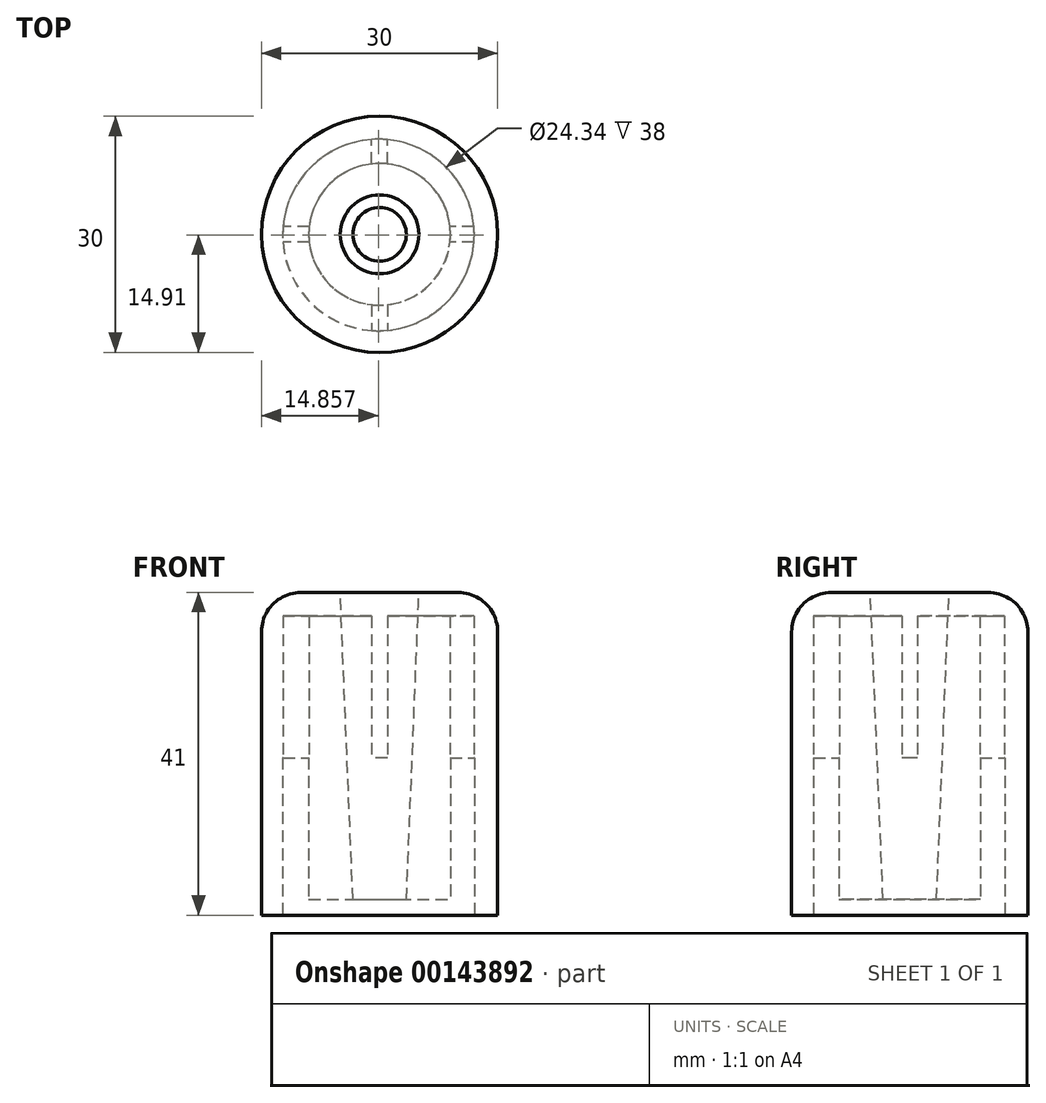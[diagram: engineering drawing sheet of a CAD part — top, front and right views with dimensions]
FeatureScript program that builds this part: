
annotation { "Feature Type Name" : "Feature", "Feature Type Description" : "" }
export const myFeature = defineFeature(function(context is Context, id is Id, definition is map)
    precondition{}
    {
        {
            var Q0;
            Q0=qCreatedBy(makeId("Top.planeOp"),FACE);
            var sketch = newSketch(context, id + "F0", { "sketchPlane" : qUnion([Q0])});
            skCircle(sketch, "E0", {"center": v(0, 0) * mm, "radius": 15 * mm});
            skCircle(sketch, "E1", {"center": v(-0.14, -0.1) * mm, "radius": 12.17 * mm});
            skSolve(sketch);
        }
        {
            var Q0;
            Q0=qSketchRegion(id+"F0",true);
            extrude(context, id + "F1", {"entities" : qUnion([Q0]), "depth" : 38 * mm});
        }
        {
            var Q0;
            Q0=makeQuery(id+"F1.opExtrude","CAP_FACE",FACE,{"disambiguationData":[OSD([sQuery(id+"F0.wireOp",EDGE,"E0"),sQuery(id+"F0.wireOp",EDGE,"E1")])],"isStart":false});
            var sketch = newSketch(context, id + "F2", { "sketchPlane" : qUnion([Q0])});
            skCircle(sketch, "E2.0", {"center": v(-0.14, -0.1) * mm, "radius": 12.17 * mm});
            skCircle(sketch, "E3.0", {"center": v(0, 0) * mm, "radius": 15 * mm});
            skSolve(sketch);
        }
        {
            var Q0;
            Q0=qSketchRegion(id+"F2",true);
            var Q1;
            Q1=makeQuery(id+"F2.imprint","IMPRINT",FACE,{"disambiguationData":[TD([[makeQuery(id+"F2.imprint","IMPRINT",EDGE,{"derivedFrom":sQuery(id+"F2.wireOp",EDGE,"E2.0")}),1.0]])]});
            extrude(context, id + "F3", {"entities" : qUnion([Q0, Q1]), "operationType" : NewBodyOperationType.ADD, "depth" : 3 * mm});
        }
        {
            var Q0;
            Q0=makeQuery(id+"F3.opExtrude","CAP_EDGE",EDGE,{"disambiguationData":[OSD([sQuery(id+"F2.wireOp",EDGE,"E3.0")])],"isStart":false});
            fillet(context, id + "F4", {"entities" : qUnion([Q0]), "radius" : 5 * mm, "tangentPropagation" : true, "allowEdgeOverflow" : false});
        }
        {
            var Q0;
            Q0=makeQuery(id+"F3.opExtrude","CAP_FACE",FACE,{"disambiguationData":[OSD([sQuery(id+"F2.wireOp",EDGE,"E3.0")])],"isStart":false});
            var sketch = newSketch(context, id + "F5", { "sketchPlane" : qUnion([Q0])});
            skCircle(sketch, "E4", {"center": v(0, 0) * mm, "radius": 5 * mm});
            skSolve(sketch);
        }
        {
            var Q0;
            Q0=qSketchRegion(id+"F5",true);
            extrude(context, id + "F6", {"entities" : qUnion([Q0]), "operationType" : NewBodyOperationType.ADD, "oppositeDirection" : true, "depth" : 39 * mm});
        }
        {
            var Q0;
            Q0=makeQuery(id+"F6.opExtrude","CAP_FACE",FACE,{"disambiguationData":[OSD([sQuery(id+"F5.wireOp",EDGE,"E4")])],"isStart":false});
            var sketch = newSketch(context, id + "F7", { "sketchPlane" : qUnion([Q0])});
            skCircle(sketch, "E5", {"center": v(0, 0) * mm, "radius": 3.4 * mm});
            skSolve(sketch);
        }
        {
            var Q1;
            Q1=makeQuery(id+"F5.imprint","IMPRINT",FACE,{"disambiguationData":[TD([[makeQuery(id+"F5.imprint","IMPRINT",EDGE,{"derivedFrom":sQuery(id+"F5.wireOp",EDGE,"E4")}),1.0]])]});
            var Q2;
            Q2=makeQuery(id+"F7.imprint","IMPRINT",FACE,{"disambiguationData":[TD([[makeQuery(id+"F7.imprint","IMPRINT",EDGE,{"derivedFrom":sQuery(id+"F7.wireOp",EDGE,"E5")}),1.0]])]});
            loft(context, id + "F8", {"operationType" : NewBodyOperationType.REMOVE, "sheetProfilesArray" : [{ "sheetProfileEntities" : qUnion([Q1]) }, { "sheetProfileEntities" : qUnion([Q2]) }]});
        }
        {
            var Q0;
            Q0=makeQuery(id+"F6.opExtrude","CAP_FACE",FACE,{"disambiguationData":[OSD([sQuery(id+"F5.wireOp",EDGE,"E4")])],"isStart":false});
            var sketch = newSketch(context, id + "F9", { "sketchPlane" : qUnion([Q0])});
            skCircle(sketch, "E6", {"center": v(0, 0) * mm, "radius": 9 * mm});
            skCircle(sketch, "E7.0", {"center": v(0, 0) * mm, "radius": 5 * mm});
            skSolve(sketch);
        }
        {
            var Q0;
            Q0=qSketchRegion(id+"F9",true);
            var Q1;
            Q1=makeQuery(id+"F3.opExtrude","CAP_FACE",FACE,{"disambiguationData":[OSD([sQuery(id+"F2.wireOp",EDGE,"E3.0")])],"isStart":true});
            extrude(context, id + "F10", {"entities" : qUnion([Q0]), "operationType" : NewBodyOperationType.ADD, "endBound" : BoundingType.UP_TO_SURFACE, "oppositeDirection" : true, "endBoundEntityFace" : qUnion([Q1]), "depth" : 39 * mm});
        }
        {
            var Q0;
            Q0=qCreatedBy(makeId("Top.planeOp"),FACE);
            cPlane(context, id + "F11", {"entities" : qUnion([Q0]), "cplaneType" : CPlaneType.OFFSET, "offset" : 20 * mm, "width" : 150 * mm, "height" : 150 * mm});
        }
        {
            var Q0;
            Q0=qCreatedBy(id+"F11.planeOp",FACE);
            var sketch = newSketch(context, id + "F12", { "sketchPlane" : qUnion([Q0])});
            skCircle(sketch, "E8.0", {"center": v(-0.14, -0.1) * mm, "radius": 12.17 * mm});
            skLineSegment(sketch, "E9", {"start": v(-12.31, 0) * mm, "end": v(-5, 0) * mm, "construction": true});
            skLineSegment(sketch, "E10", {"start": v(0, -12.26) * mm, "end": v(0, -5) * mm, "construction": true});
            skArc(sketch, "E11.0.startCap", {"start": v(1, -12.26) * mm, "mid": v(0, -13.26) * mm, "end": v(-1, -12.26) * mm});
            skArc(sketch, "E11.0.endCap", {"start": v(-1, 12.08) * mm, "mid": v(0, 13.08) * mm, "end": v(1, 12.08) * mm});
            skLineSegment(sketch, "E11.0.left", {"start": v(-1, -12.26) * mm, "end": v(-1, -4.9) * mm});
            skLineSegment(sketch, "E11.0.right", {"start": v(1, -12.26) * mm, "end": v(1, -4.9) * mm});
            skArc(sketch, "E11.1.startCap", {"start": v(-12.31, -1) * mm, "mid": v(-13.31, 0) * mm, "end": v(-12.31, 1) * mm});
            skArc(sketch, "E11.1.endCap", {"start": v(12.03, 1) * mm, "mid": v(13.03, 0) * mm, "end": v(12.03, -1) * mm});
            skLineSegment(sketch, "E11.1.left", {"start": v(-12.31, 1) * mm, "end": v(-4.9, 1) * mm});
            skLineSegment(sketch, "E11.1.right", {"start": v(-12.31, -1) * mm, "end": v(-4.9, -1) * mm});
            skCircle(sketch, "E12.0.0", {"center": v(0, 0) * mm, "radius": 5 * mm});
            skLineSegment(sketch, "E13.trimOffspring", {"start": v(-1, -1) * mm, "end": v(1, -1) * mm});
            skLineSegment(sketch, "E14.trimOffspring", {"start": v(-1, 0) * mm, "end": v(12.03, 0) * mm, "construction": true});
            skLineSegment(sketch, "E15.trimOffspring", {"start": v(-1, 1) * mm, "end": v(1, 1) * mm});
            skLineSegment(sketch, "E16.trimOffspring", {"start": v(-1, -1) * mm, "end": v(-1, 1) * mm});
            skLineSegment(sketch, "E17.trimOffspring", {"start": v(0, -1) * mm, "end": v(0, 12.08) * mm, "construction": true});
            skLineSegment(sketch, "E18.trimOffspring", {"start": v(1, -1) * mm, "end": v(1, 1) * mm});
            skLineSegment(sketch, "E19.trimOffspring", {"start": v(4.9, -1) * mm, "end": v(12.03, -1) * mm});
            skLineSegment(sketch, "E20.trimOffspring", {"start": v(4.9, 1) * mm, "end": v(12.03, 1) * mm});
            skLineSegment(sketch, "E21.trimOffspring", {"start": v(1, 4.9) * mm, "end": v(1, 12.08) * mm});
            skLineSegment(sketch, "E22.trimOffspring", {"start": v(-1, 4.9) * mm, "end": v(-1, 12.08) * mm});
            skSolve(sketch);
        }
        {
            var Q0;
            {var subQ0=sQuery(id+"F12.wireOp",EDGE,"E11.1.left");var subQ1=sQuery(id+"F12.wireOp",EDGE,"E8.0");var subQ2=makeQuery(id+"F12.imprint","INTERSECT",VERTEX,{"derivedFrom":[subQ1,subQ0]});Q0=makeQuery(id+"F12.imprint","IMPRINT",FACE,{"disambiguationData":[TD([[makeQuery(id+"F12.imprint","IMPRINT",EDGE,{"disambiguationData":[TD([[subQ2,-1.0]])],"derivedFrom":subQ1}),1.0]])]});}
            var Q1;
            {var subQ0=sQuery(id+"F12.wireOp",EDGE,"E20.trimOffspring");var subQ1=sQuery(id+"F12.wireOp",EDGE,"E8.0");var subQ2=makeQuery(id+"F12.imprint","INTERSECT",VERTEX,{"derivedFrom":[subQ1,subQ0]});Q1=makeQuery(id+"F12.imprint","IMPRINT",FACE,{"disambiguationData":[TD([[makeQuery(id+"F12.imprint","IMPRINT",EDGE,{"disambiguationData":[TD([[subQ2,1.0]])],"derivedFrom":subQ1}),1.0]])]});}
            var Q2;
            {var subQ0=sQuery(id+"F12.wireOp",EDGE,"E11.0.left");var subQ1=sQuery(id+"F12.wireOp",EDGE,"E8.0");var subQ2=makeQuery(id+"F12.imprint","INTERSECT",VERTEX,{"derivedFrom":[subQ1,subQ0]});Q2=makeQuery(id+"F12.imprint","IMPRINT",FACE,{"disambiguationData":[TD([[makeQuery(id+"F12.imprint","IMPRINT",EDGE,{"disambiguationData":[TD([[subQ2,-1.0]])],"derivedFrom":subQ1}),1.0]])]});}
            var Q3;
            {var subQ0=sQuery(id+"F12.wireOp",EDGE,"E21.trimOffspring");var subQ1=sQuery(id+"F12.wireOp",EDGE,"E8.0");var subQ2=makeQuery(id+"F12.imprint","INTERSECT",VERTEX,{"derivedFrom":[subQ1,subQ0]});Q3=makeQuery(id+"F12.imprint","IMPRINT",FACE,{"disambiguationData":[TD([[makeQuery(id+"F12.imprint","IMPRINT",EDGE,{"disambiguationData":[TD([[subQ2,-1.0]])],"derivedFrom":subQ1}),1.0]])]});}
            extrude(context, id + "F13", {"entities" : qUnion([Q0, Q1, Q2, Q3]), "operationType" : NewBodyOperationType.ADD, "endBound" : BoundingType.UP_TO_NEXT, "depth" : 25 * mm});
        }
    });
